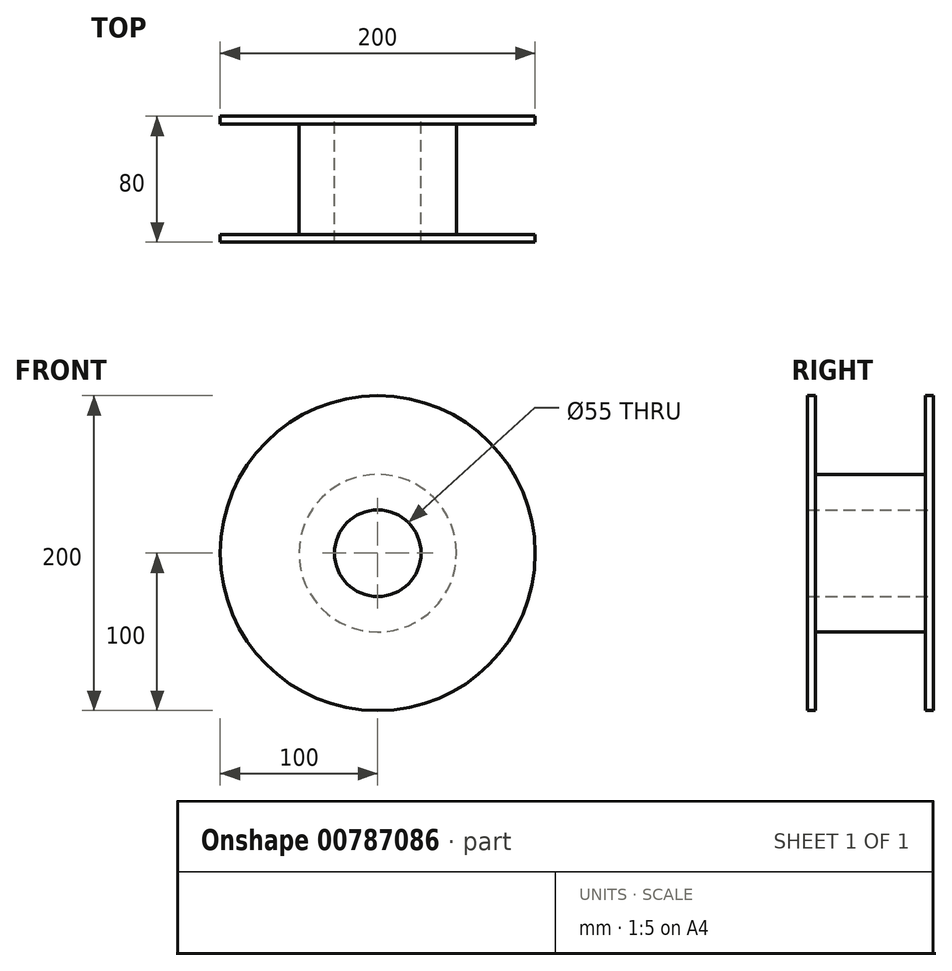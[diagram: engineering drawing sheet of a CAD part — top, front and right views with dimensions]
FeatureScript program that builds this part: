
annotation { "Feature Type Name" : "Feature", "Feature Type Description" : "" }
export const myFeature = defineFeature(function(context is Context, id is Id, definition is map)
    precondition{}
    {
        {
            var Q0;
            Q0=qCreatedBy(makeId("Front.planeOp"),FACE);
            var sketch = newSketch(context, id + "F0", { "sketchPlane" : qUnion([Q0])});
            skCircle(sketch, "E0", {"center": v(0, 0) * mm, "radius": 50 * mm});
            skSolve(sketch);
        }
        {
            var Q0;
            Q0 = qSketchRegion(id + "F0", true);
            extrude(context, id + "F1", {"entities" : qUnion([Q0]), "depth" : 80 * mm, "offsetDistance" : 25 * mm});
        }
        {
            var Q0;
            Q0=qCreatedBy(makeId("Front.planeOp"),FACE);
            var sketch = newSketch(context, id + "F2", { "sketchPlane" : qUnion([Q0])});
            skCircle(sketch, "E1", {"center": v(0, 0) * mm, "radius": 100 * mm});
            skSolve(sketch);
        }
        {
            var Q0;
            Q0 = qSketchRegion(id + "F2", true);
            extrude(context, id + "F3", {"entities" : qUnion([Q0]), "operationType" : NewBodyOperationType.ADD, "depth" : 5 * mm, "offsetDistance" : 25 * mm});
        }
        {
            var Q0;
            Q0=makeQuery(id+"F1.opExtrude","CAP_FACE",FACE,{"disambiguationData":[OSD([sQuery(id+"F0.wireOp",EDGE,"E0")])],"isStart":false});
            var sketch = newSketch(context, id + "F4", { "sketchPlane" : qUnion([Q0])});
            skCircle(sketch, "E2", {"center": v(0, 0) * mm, "radius": 100 * mm});
            skSolve(sketch);
        }
        {
            var Q0;
            Q0 = qSketchRegion(id + "F4", true);
            extrude(context, id + "F5", {"entities" : qUnion([Q0]), "operationType" : NewBodyOperationType.ADD, "oppositeDirection" : true, "depth" : 5 * mm, "offsetDistance" : 25 * mm});
        }
        {
            var Q0;
            Q0=makeQuery(id+"F3.boolean.opBoolean","MERGE",FACE,{"derivedFrom":[makeQuery(id+"F1.opExtrude","CAP_FACE",FACE,{"disambiguationData":[OSD([sQuery(id+"F0.wireOp",EDGE,"E0")])],"isStart":true}),makeQuery(id+"F3.opExtrude","CAP_FACE",FACE,{"disambiguationData":[OSD([sQuery(id+"F2.wireOp",EDGE,"E1")])],"isStart":true})]});
            var sketch = newSketch(context, id + "F6", { "sketchPlane" : qUnion([Q0])});
            skCircle(sketch, "E3", {"center": v(0, 0) * mm, "radius": 27.5 * mm});
            skSolve(sketch);
        }
        {
            var Q0;
            Q0 = qSketchRegion(id + "F6", true);
            extrude(context, id + "F7", {"entities" : qUnion([Q0]), "operationType" : NewBodyOperationType.REMOVE, "oppositeDirection" : true, "depth" : 100 * mm, "offsetDistance" : 25 * mm});
        }
    });
